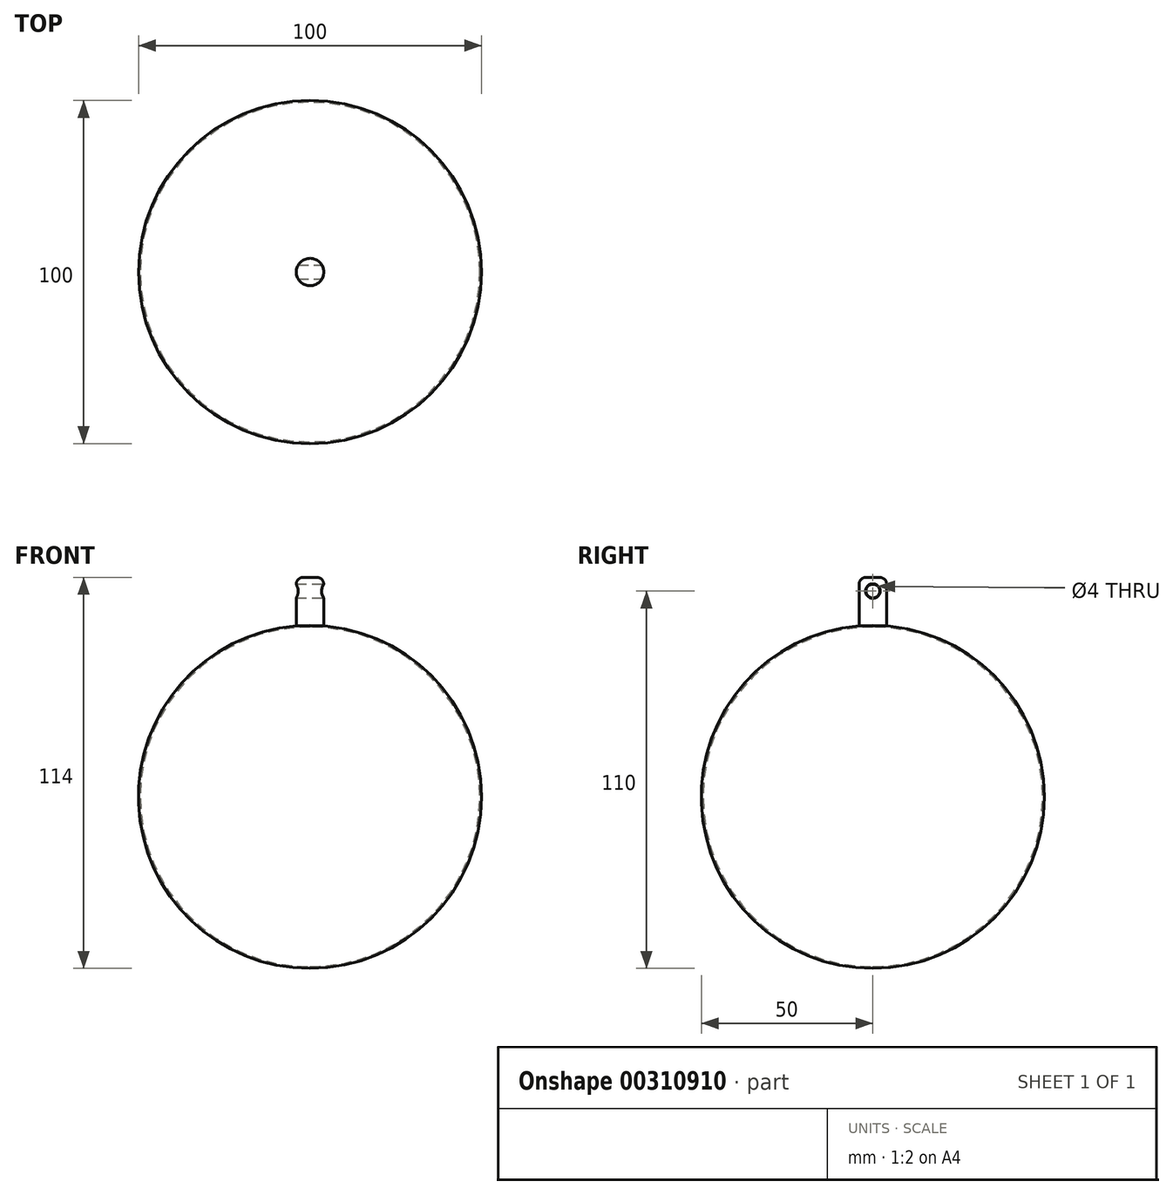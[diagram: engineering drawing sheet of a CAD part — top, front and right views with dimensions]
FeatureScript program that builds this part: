
annotation { "Feature Type Name" : "Feature", "Feature Type Description" : "" }
export const myFeature = defineFeature(function(context is Context, id is Id, definition is map)
    precondition{}
    {
        {
            var Q0;
            Q0=qCreatedBy(makeId("Front.planeOp"),FACE);
            var sketch = newSketch(context, id + "F0", { "sketchPlane" : qUnion([Q0])});
            skLineSegment(sketch, "E0", {"start": v(0, 50) * mm, "end": v(0, -50) * mm, "construction": true});
            skArc(sketch, "E1", {"start": v(0, 50) * mm, "mid": v(-50, 0) * mm, "end": v(0, -50) * mm});
            skArc(sketch, "E2", {"start": v(0, 49.5) * mm, "mid": v(-49.5, 0) * mm, "end": v(0, -49.5) * mm});
            skLineSegment(sketch, "E3", {"start": v(0, 50) * mm, "end": v(0, 49.5) * mm});
            skLineSegment(sketch, "E4", {"start": v(0, -49.5) * mm, "end": v(0, -50) * mm});
            skSolve(sketch);
        }
        {
            var Q0;
            Q0 = qSketchRegion(id + "F0", true);
            var Q1;
            Q1=sQuery(id+"F0.wireOp",EDGE,"E0");
            revolve(context, id + "F1", {"entities" : qUnion([Q0]), "axis" : qUnion([Q1]), "revolveType" : RevolveType.FULL});
        }
        {
            var Q0;
            Q0=qCreatedBy(makeId("Right.planeOp"),FACE);
            var sketch = newSketch(context, id + "F2", { "sketchPlane" : qUnion([Q0])});
            skArc(sketch, "E5", {"start": v(0, 50) * mm, "mid": v(-2, 49.96) * mm, "end": v(-4, 49.84) * mm});
            skLineSegment(sketch, "E6.top", {"start": v(-4, 64) * mm, "end": v(0, 64) * mm});
            skLineSegment(sketch, "E6.left", {"start": v(-4, 49.84) * mm, "end": v(-4, 64) * mm});
            skLineSegment(sketch, "E7", {"start": v(0, 64) * mm, "end": v(0, 50) * mm});
            skPoint(sketch, "E6.right.end.orphan", {"position": v(4, 64) * mm});
            skLineSegment(sketch, "E8", {"start": v(0, 46.37) * mm, "end": v(0, 67.46) * mm, "construction": true});
            skSolve(sketch);
        }
        {
            var Q0;
            Q0 = qSketchRegion(id + "F2", true);
            var Q1;
            Q1=sQuery(id+"F2.wireOp",EDGE,"E8");
            revolve(context, id + "F3", {"entities" : qUnion([Q0]), "axis" : qUnion([Q1]), "revolveType" : RevolveType.FULL});
        }
        {
            var Q0;
            Q0=qCreatedBy(makeId("Right.planeOp"),FACE);
            var sketch = newSketch(context, id + "F4", { "sketchPlane" : qUnion([Q0])});
            skCircle(sketch, "E9", {"center": v(0, 60) * mm, "radius": 2 * mm});
            skSolve(sketch);
        }
        {
            var Q0;
            Q0 = qSketchRegion(id + "F4", true);
            extrude(context, id + "F5", {"entities" : qUnion([Q0]), "operationType" : NewBodyOperationType.REMOVE, "endBound" : BoundingType.SYMMETRIC, "oppositeDirection" : true, "depth" : 25 * mm});
        }
        {
            var Q0;
            Q0=makeQuery(id+"F3.opRevolve","SWEPT_EDGE",EDGE,{"disambiguationData":[OSD([sQuery(id+"F2.wireOp",EDGE,"E6.top"),sQuery(id+"F2.wireOp",EDGE,"E6.left")])]});
            fillet(context, id + "F6", {"entities" : qUnion([Q0]), "radius" : 2 * mm, "tangentPropagation" : true, "allowEdgeOverflow" : false});
        }
        {
            var Q0;
            Q0=makeQuery(id+"F5.boolean.opBoolean","INTERSECT",EDGE,{"disambiguationData":[OD(1.0)],"derivedFrom":[makeQuery(id+"F3.opRevolve","SWEPT_FACE",FACE,{"disambiguationData":[OSD([sQuery(id+"F2.wireOp",EDGE,"E6.left")])]}),makeQuery(id+"F5.opExtrude","SWEPT_FACE",FACE,{"disambiguationData":[OSD([sQuery(id+"F4.wireOp",EDGE,"E9")])]})]});
            fillet(context, id + "F7", {"entities" : qUnion([Q0]), "radius" : 0.1 * mm, "tangentPropagation" : true, "allowEdgeOverflow" : false});
        }
    });
